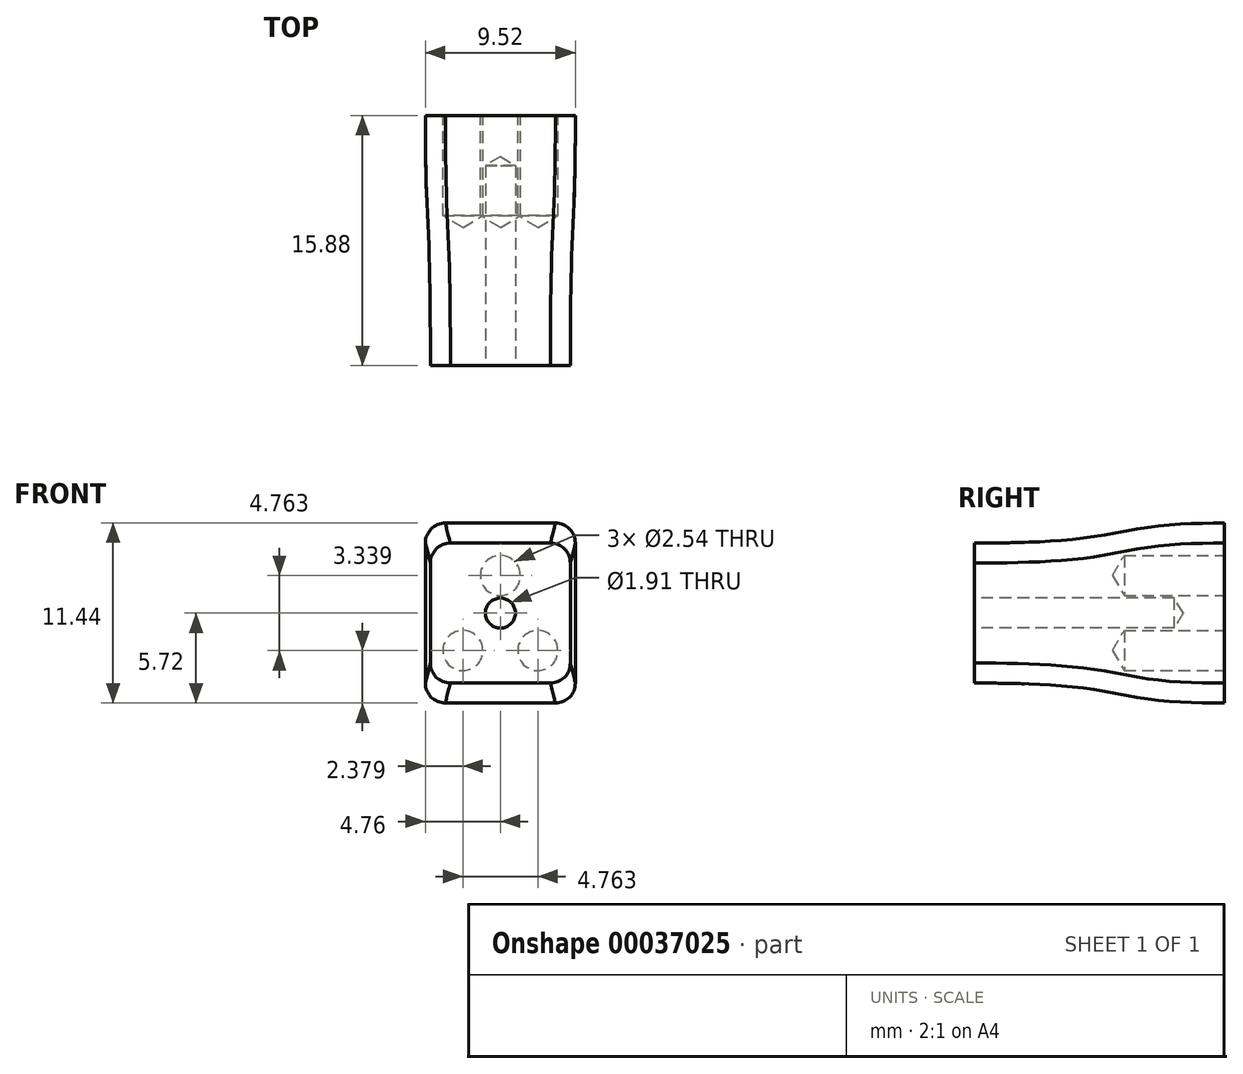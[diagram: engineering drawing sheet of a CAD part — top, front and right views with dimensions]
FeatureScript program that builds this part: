
annotation { "Feature Type Name" : "Feature", "Feature Type Description" : "" }
export const myFeature = defineFeature(function(context is Context, id is Id, definition is map)
    precondition{}
    {
        {
            var Q0;
            Q0=qCreatedBy(makeId("Front.planeOp"),FACE);
            var sketch = newSketch(context, id + "F0", { "sketchPlane" : qUnion([Q0])});
            skLineSegment(sketch, "E0.rect.bottom", {"start": v(4.76, 5.72) * mm, "end": v(-4.76, 5.72) * mm});
            skLineSegment(sketch, "E0.rect.top", {"start": v(4.76, -5.72) * mm, "end": v(-4.76, -5.72) * mm});
            skLineSegment(sketch, "E0.rect.left", {"start": v(4.76, 5.71) * mm, "end": v(4.76, -5.72) * mm});
            skLineSegment(sketch, "E0.rect.right", {"start": v(-4.76, 5.72) * mm, "end": v(-4.76, -5.72) * mm});
            skPoint(sketch, "E0.rect.middle", {"position": v(0, 0) * mm});
            skSolve(sketch);
        }
        {
            var Q0;
            Q0=qCreatedBy(makeId("Front.planeOp"),FACE);
            cPlane(context, id + "F1", {"entities" : qUnion([Q0]), "cplaneType" : CPlaneType.OFFSET, "offset" : 15.88 * mm, "width" : 152.4 * mm, "height" : 152.4 * mm});
        }
        {
            var Q0;
            Q0=qCreatedBy(id+"F1.planeOp",FACE);
            var sketch = newSketch(context, id + "F2", { "sketchPlane" : qUnion([Q0])});
            skLineSegment(sketch, "E1.rect.bottom", {"start": v(4.44, 4.45) * mm, "end": v(-4.45, 4.45) * mm});
            skLineSegment(sketch, "E1.rect.top", {"start": v(4.45, -4.44) * mm, "end": v(-4.45, -4.45) * mm});
            skLineSegment(sketch, "E1.rect.left", {"start": v(4.44, 4.45) * mm, "end": v(4.45, -4.45) * mm});
            skLineSegment(sketch, "E1.rect.right", {"start": v(-4.45, 4.44) * mm, "end": v(-4.45, -4.45) * mm});
            skPoint(sketch, "E1.rect.middle", {"position": v(0, 0) * mm});
            skSolve(sketch);
        }
        {
            var Q0;
            Q0=makeQuery(id+"F0.imprint","IMPRINT",FACE,{"disambiguationData":[TD([[makeQuery(id+"F0.imprint","IMPRINT",EDGE,{"derivedFrom":sQuery(id+"F0.wireOp",EDGE,"E0.rect.bottom")}),1.0]])]});
            var Q1;
            Q1=makeQuery(id+"F2.imprint","IMPRINT",FACE,{"disambiguationData":[TD([[makeQuery(id+"F2.imprint","IMPRINT",EDGE,{"derivedFrom":sQuery(id+"F2.wireOp",EDGE,"E1.rect.bottom")}),1.0]])]});
            loft(context, id + "F3", {"startCondition" : LoftEndDerivativeType.NORMAL_TO_PROFILE, "startMagnitude" : 1.5, "endCondition" : LoftEndDerivativeType.NORMAL_TO_PROFILE, "endMagnitude" : 2, "sheetProfilesArray" : [{ "sheetProfileEntities" : qUnion([Q0]) }, { "sheetProfileEntities" : qUnion([Q1]) }]});
        }
        {
            var Q0;
            Q0=makeQuery(id+"F3.opLoft","CAP_FACE",FACE,{"disambiguationData":[OSD([makeQuery(id+"F0.imprint","IMPRINT",FACE,{"disambiguationData":[TD([[makeQuery(id+"F0.imprint","IMPRINT",EDGE,{"derivedFrom":sQuery(id+"F0.wireOp",EDGE,"E0.rect.bottom")}),1.0]])]})])],"isStart":true});
            var sketch = newSketch(context, id + "F4", { "sketchPlane" : qUnion([Q0])});
            skLineSegment(sketch, "E2", {"start": v(-2.38, -2.38) * mm, "end": v(2.38, -2.38) * mm, "construction": true});
            skLineSegment(sketch, "E3", {"start": v(0, -2.38) * mm, "end": v(0, 2.38) * mm, "construction": true});
            skPoint(sketch, "E4", {"position": v(0, 0) * mm});
            skPoint(sketch, "E5", {"position": v(0, -2.38) * mm});
            skSolve(sketch);
        }
        {
            var Q0;
            Q0=makeQuery(id+"F3.opLoft","CAP_FACE",FACE,{"disambiguationData":[OSD([makeQuery(id+"F2.imprint","IMPRINT",FACE,{"disambiguationData":[TD([[makeQuery(id+"F2.imprint","IMPRINT",EDGE,{"derivedFrom":sQuery(id+"F2.wireOp",EDGE,"E1.rect.bottom")}),1.0]])]})])],"isStart":true});
            var sketch = newSketch(context, id + "F5", { "sketchPlane" : qUnion([Q0])});
            skPoint(sketch, "E6", {"position": v(0, 0) * mm});
            skSolve(sketch);
        }
        {
            var Q0;
            Q0=sQuery(id+"F4.wireOp",VERTEX,"E2.start");
            var Q1;
            Q1=sQuery(id+"F4.wireOp",VERTEX,"E2.end");
            var Q2;
            Q2=sQuery(id+"F4.wireOp",VERTEX,"E3.end");
            var Q3;
            Q3=makeQuery(id+"F3.opLoft","SWEPT_BODY",BODY,{"disambiguationData":[OSD([makeQuery(id+"F0.imprint","IMPRINT",FACE,{"disambiguationData":[TD([[makeQuery(id+"F0.imprint","IMPRINT",EDGE,{"derivedFrom":sQuery(id+"F0.wireOp",EDGE,"E0.rect.bottom")}),1.0]])]}),makeQuery(id+"F2.imprint","IMPRINT",FACE,{"disambiguationData":[TD([[makeQuery(id+"F2.imprint","IMPRINT",EDGE,{"derivedFrom":sQuery(id+"F2.wireOp",EDGE,"E1.rect.bottom")}),1.0]])]})])]});
            hole(context, id + "F6", {"style" : HoleStyle.SIMPLE, "holeDiameter" : 2.54 * mm, "endStyle" : HoleEndStyle.BLIND, "holeDepth" : 6.35 * mm, "locations" : qUnion([Q0, Q1, Q2]), "scope" : qUnion([Q3])});
        }
        {
            var Q0;
            Q0=sQuery(id+"F5.wireOp",VERTEX,"E6");
            var Q1;
            Q1=makeQuery(id+"F3.opLoft","SWEPT_BODY",BODY,{"disambiguationData":[OSD([makeQuery(id+"F0.imprint","IMPRINT",FACE,{"disambiguationData":[TD([[makeQuery(id+"F0.imprint","IMPRINT",EDGE,{"derivedFrom":sQuery(id+"F0.wireOp",EDGE,"E0.rect.bottom")}),1.0]])]}),makeQuery(id+"F2.imprint","IMPRINT",FACE,{"disambiguationData":[TD([[makeQuery(id+"F2.imprint","IMPRINT",EDGE,{"derivedFrom":sQuery(id+"F2.wireOp",EDGE,"E1.rect.bottom")}),1.0]])]})])]});
            hole(context, id + "F7", {"style" : HoleStyle.SIMPLE, "holeDiameter" : 1.9 * mm, "endStyle" : HoleEndStyle.BLIND, "holeDepth" : 12.7 * mm, "locations" : qUnion([Q0]), "scope" : qUnion([Q1])});
        }
        {
            var Q0;
            Q0=makeQuery(id+"F3.opLoft","SWEPT_EDGE",EDGE,{"disambiguationData":[OSD([sQuery(id+"F0.wireOp",EDGE,"E0.rect.bottom"),sQuery(id+"F0.wireOp",EDGE,"E0.rect.left"),sQuery(id+"F2.wireOp",EDGE,"E1.rect.bottom"),sQuery(id+"F2.wireOp",EDGE,"E1.rect.left")])]});
            var Q1;
            Q1=makeQuery(id+"F3.opLoft","SWEPT_EDGE",EDGE,{"disambiguationData":[OSD([sQuery(id+"F0.wireOp",EDGE,"E0.rect.bottom"),sQuery(id+"F0.wireOp",EDGE,"E0.rect.right"),sQuery(id+"F2.wireOp",EDGE,"E1.rect.bottom"),sQuery(id+"F2.wireOp",EDGE,"E1.rect.right")])]});
            var Q2;
            Q2=makeQuery(id+"F3.opLoft","SWEPT_EDGE",EDGE,{"disambiguationData":[OSD([sQuery(id+"F0.wireOp",EDGE,"E0.rect.top"),sQuery(id+"F0.wireOp",EDGE,"E0.rect.left"),sQuery(id+"F2.wireOp",EDGE,"E1.rect.top"),sQuery(id+"F2.wireOp",EDGE,"E1.rect.left")])]});
            var Q3;
            Q3=makeQuery(id+"F3.opLoft","SWEPT_EDGE",EDGE,{"disambiguationData":[OSD([sQuery(id+"F0.wireOp",EDGE,"E0.rect.top"),sQuery(id+"F0.wireOp",EDGE,"E0.rect.right"),sQuery(id+"F2.wireOp",EDGE,"E1.rect.top"),sQuery(id+"F2.wireOp",EDGE,"E1.rect.right")])]});
            fillet(context, id + "F8", {"entities" : qUnion([Q0, Q1, Q2, Q3]), "radius" : 1.27 * mm, "tangentPropagation" : true, "allowEdgeOverflow" : false});
        }
    });
